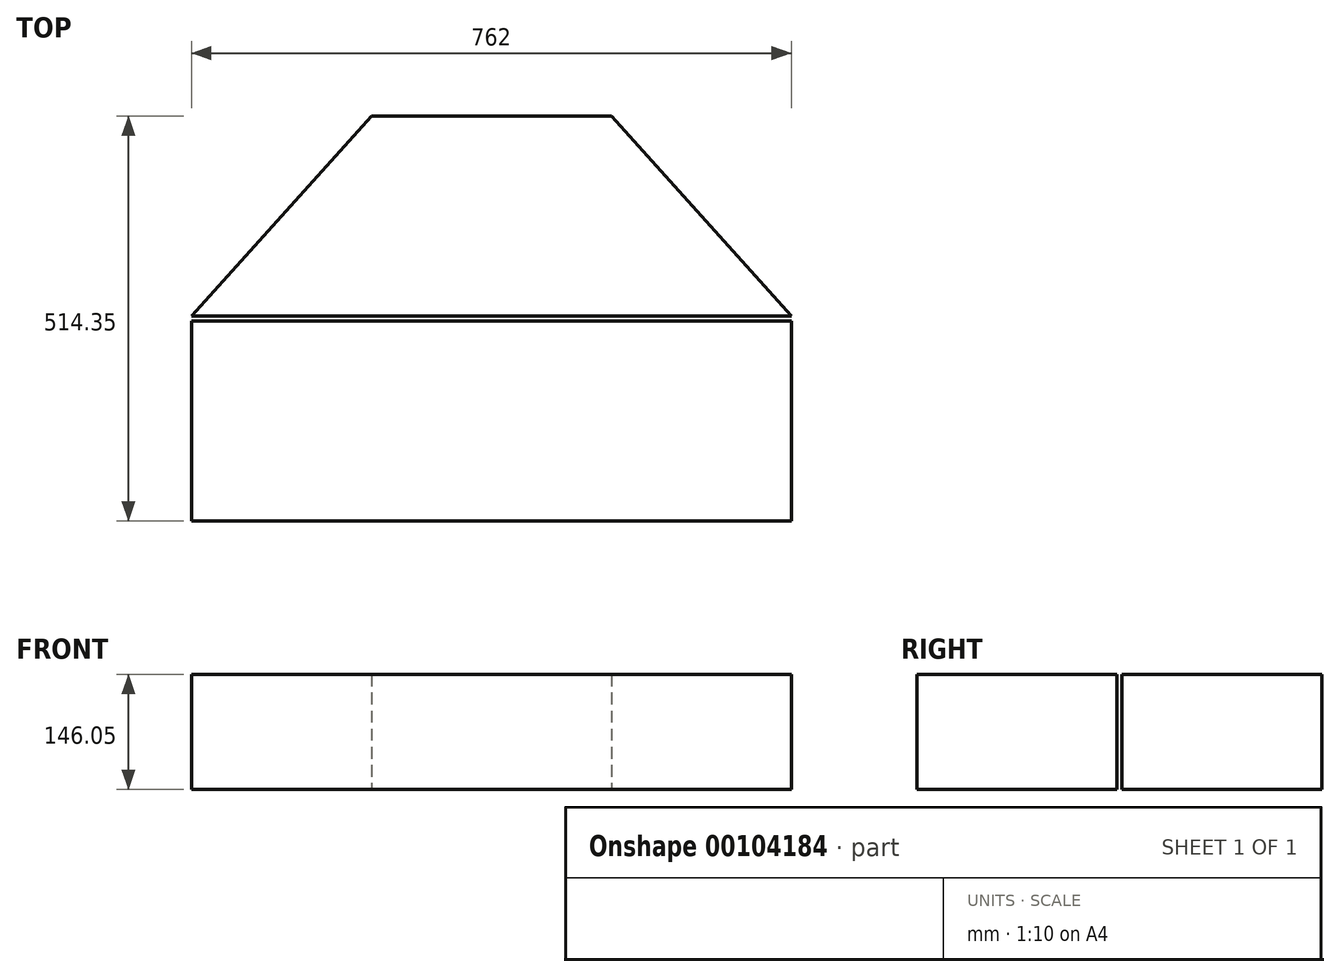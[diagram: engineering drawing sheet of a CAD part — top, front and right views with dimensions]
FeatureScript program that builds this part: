
annotation { "Feature Type Name" : "Feature", "Feature Type Description" : "" }
export const myFeature = defineFeature(function(context is Context, id is Id, definition is map)
    precondition{}
    {
        {
            var Q0;
            Q0=qCreatedBy(makeId("Top.planeOp"),FACE);
            var sketch = newSketch(context, id + "F0", { "sketchPlane" : qUnion([Q0])});
            skLineSegment(sketch, "E0.bottom", {"start": v(-362.86, -147.1) * mm, "end": v(399.14, -147.1) * mm});
            skLineSegment(sketch, "E0.top", {"start": v(-362.86, 106.9) * mm, "end": v(399.14, 106.9) * mm});
            skLineSegment(sketch, "E0.left", {"start": v(-362.86, -147.1) * mm, "end": v(-362.86, 106.9) * mm});
            skLineSegment(sketch, "E0.right", {"start": v(399.14, -147.1) * mm, "end": v(399.14, 106.9) * mm});
            skSolve(sketch);
        }
        {
            var Q0;
            Q0=makeQuery(id+"F0.imprint","IMPRINT",FACE,{"disambiguationData":[TD([[makeQuery(id+"F0.imprint","IMPRINT",EDGE,{"derivedFrom":sQuery(id+"F0.wireOp",EDGE,"E0.bottom")}),1.0]])]});
            extrude(context, id + "F1", {"entities" : qUnion([Q0]), "depth" : 146.05 * mm});
        }
        {
            var Q0;
            Q0=qCreatedBy(makeId("Top.planeOp"),FACE);
            var sketch = newSketch(context, id + "F2", { "sketchPlane" : qUnion([Q0])});
            skLineSegment(sketch, "E1", {"start": v(-362.86, 113.24) * mm, "end": v(399.14, 113.24) * mm});
            skLineSegment(sketch, "E2", {"start": v(399.14, 113.24) * mm, "end": v(170.54, 367.24) * mm});
            skLineSegment(sketch, "E3", {"start": v(170.54, 367.24) * mm, "end": v(-134.26, 367.24) * mm});
            skLineSegment(sketch, "E4", {"start": v(-134.26, 367.24) * mm, "end": v(-362.86, 113.24) * mm});
            skSolve(sketch);
        }
        {
            var Q0;
            Q0 = qSketchRegion(id + "F2", true);
            extrude(context, id + "F3", {"entities" : qUnion([Q0]), "depth" : 146.05 * mm});
        }
    });
